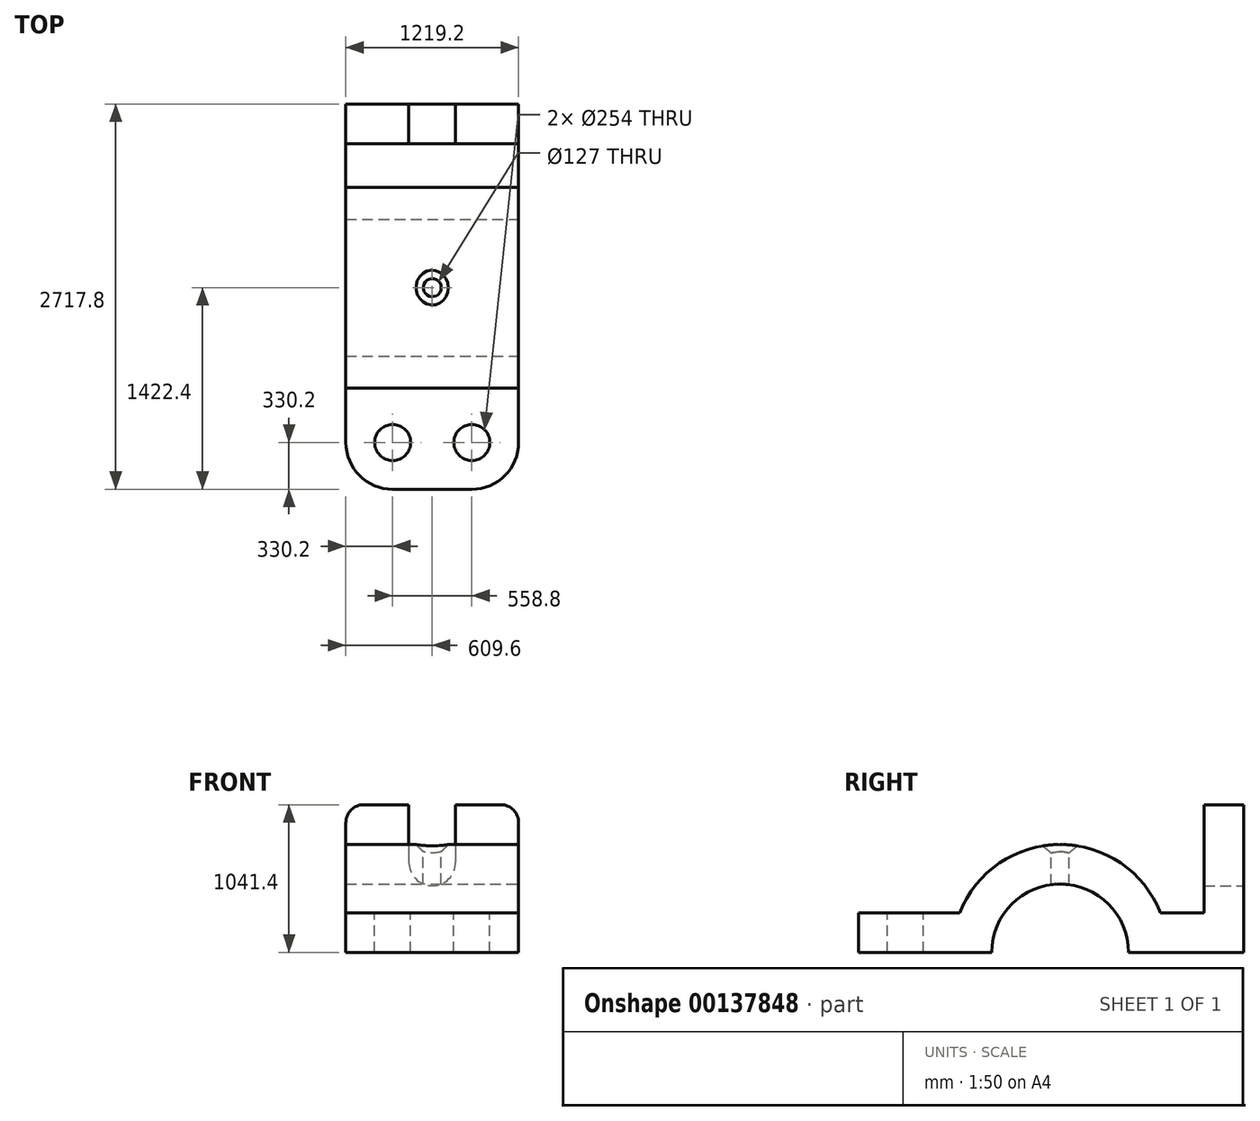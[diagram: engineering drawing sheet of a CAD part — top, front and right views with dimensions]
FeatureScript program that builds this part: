
annotation { "Feature Type Name" : "Feature", "Feature Type Description" : "" }
export const myFeature = defineFeature(function(context is Context, id is Id, definition is map)
    precondition{}
    {
        {
            var Q0;
            Q0=qCreatedBy(makeId("Top.planeOp"),FACE);
            var sketch = newSketch(context, id + "F0", { "sketchPlane" : qUnion([Q0])});
            skLineSegment(sketch, "E0", {"start": v(0, 0) * mm, "end": v(0, 2717.8) * mm});
            skLineSegment(sketch, "E1", {"start": v(0, 2717.8) * mm, "end": v(-1219.2, 2717.8) * mm});
            skLineSegment(sketch, "E2", {"start": v(-1219.2, 2717.8) * mm, "end": v(-1219.2, 0) * mm});
            skLineSegment(sketch, "E3", {"start": v(-1219.2, 0) * mm, "end": v(0, 0) * mm});
            skSolve(sketch);
        }
        {
            var Q0;
            Q0 = qSketchRegion(id + "F0", true);
            extrude(context, id + "F1", {"entities" : qUnion([Q0]), "depth" : 1041.4 * mm});
        }
        {
            var Q0;
            Q0=qCreatedBy(makeId("Right.planeOp"),FACE);
            var sketch = newSketch(context, id + "F2", { "sketchPlane" : qUnion([Q0])});
            skLineSegment(sketch, "E4", {"start": v(0, 0) * mm, "end": v(1422.4, 0) * mm});
            skLineSegment(sketch, "E5", {"start": v(1422.4, 0) * mm, "end": v(1905, 0) * mm});
            skLineSegment(sketch, "E6", {"start": v(1422.4, 0) * mm, "end": v(939.8, 0) * mm});
            skArc(sketch, "E7", {"start": v(1905, 0) * mm, "mid": v(1422.4, 481.35) * mm, "end": v(939.8, 0) * mm});
            skSolve(sketch);
        }
        {
            var Q0;
            Q0=makeQuery(id+"F2.imprint","IMPRINT",FACE,{"disambiguationData":[TD([[makeQuery(id+"F2.imprint","IMPRINT",EDGE,{"derivedFrom":sQuery(id+"F2.wireOp",EDGE,"E5")}),1.0]])]});
            extrude(context, id + "F3", {"entities" : qUnion([Q0]), "operationType" : NewBodyOperationType.REMOVE, "endBound" : BoundingType.THROUGH_ALL, "oppositeDirection" : true, "depth" : 25.4 * mm});
        }
        {
            var Q0;
            Q0=makeQuery(id+"F1.opExtrude","SWEPT_FACE",FACE,{"disambiguationData":[OSD([sQuery(id+"F0.wireOp",EDGE,"E0")])]});
            var sketch = newSketch(context, id + "F4", { "sketchPlane" : qUnion([Q0])});
            skLineSegment(sketch, "E8", {"start": v(0, 1041.4) * mm, "end": v(0, 279.4) * mm});
            skLineSegment(sketch, "E9", {"start": v(0, 279.4) * mm, "end": v(713.97, 279.4) * mm});
            skLineSegment(sketch, "E10", {"start": v(0, 1041.4) * mm, "end": v(2438.4, 1041.4) * mm});
            skLineSegment(sketch, "E11", {"start": v(2438.4, 1041.4) * mm, "end": v(2438.4, 279.4) * mm});
            skLineSegment(sketch, "E12", {"start": v(2438.4, 279.4) * mm, "end": v(2130.83, 279.4) * mm});
            skArc(sketch, "E13", {"start": v(2130.83, 279.4) * mm, "mid": v(1422.4, 760.75) * mm, "end": v(713.97, 279.4) * mm});
            skSolve(sketch);
        }
        {
            var Q0;
            Q0 = qSketchRegion(id + "F4", true);
            extrude(context, id + "F5", {"entities" : qUnion([Q0]), "operationType" : NewBodyOperationType.REMOVE, "endBound" : BoundingType.THROUGH_ALL, "oppositeDirection" : true, "depth" : 25.4 * mm});
        }
        {
            var Q0;
            Q0=makeQuery(id+"F5.boolean.opBoolean","COPY",FACE,{"derivedFrom":makeQuery(id+"F5.opExtrude","SWEPT_FACE",FACE,{"disambiguationData":[OSD([sQuery(id+"F4.wireOp",EDGE,"E9")])]})});
            var sketch = newSketch(context, id + "F6", { "sketchPlane" : qUnion([Q0])});
            skCircle(sketch, "E14", {"center": v(-889, 330.2) * mm, "radius": 127 * mm});
            skCircle(sketch, "E15", {"center": v(-330.2, 330.2) * mm, "radius": 127 * mm});
            skSolve(sketch);
        }
        {
            var Q0;
            Q0 = qSketchRegion(id + "F6", true);
            extrude(context, id + "F7", {"entities" : qUnion([Q0]), "operationType" : NewBodyOperationType.REMOVE, "endBound" : BoundingType.THROUGH_ALL, "oppositeDirection" : true, "depth" : 25.4 * mm});
        }
        {
            var Q0;
            Q0=makeQuery(id+"F1.opExtrude","SWEPT_EDGE",EDGE,{"disambiguationData":[OSD([sQuery(id+"F0.wireOp",EDGE,"E2"),sQuery(id+"F0.wireOp",EDGE,"E3")])]});
            var Q1;
            Q1=makeQuery(id+"F1.opExtrude","SWEPT_EDGE",EDGE,{"disambiguationData":[OSD([sQuery(id+"F0.wireOp",EDGE,"E0"),sQuery(id+"F0.wireOp",EDGE,"E3")])]});
            fillet(context, id + "F8", {"entities" : qUnion([Q0, Q1]), "radius" : 330.2 * mm, "tangentPropagation" : true, "allowEdgeOverflow" : false});
        }
        {
            var Q0;
            Q0=makeQuery(id+"F1.opExtrude","CAP_EDGE",EDGE,{"disambiguationData":[OSD([sQuery(id+"F0.wireOp",EDGE,"E0")])],"isStart":false});
            var Q1;
            Q1=makeQuery(id+"F1.opExtrude","CAP_EDGE",EDGE,{"disambiguationData":[OSD([sQuery(id+"F0.wireOp",EDGE,"E2")])],"isStart":false});
            fillet(context, id + "F9", {"entities" : qUnion([Q0, Q1]), "radius" : 127 * mm, "tangentPropagation" : true, "allowEdgeOverflow" : false});
        }
        {
            var Q0;
            Q0=makeQuery(id+"F1.opExtrude","SWEPT_FACE",FACE,{"disambiguationData":[OSD([sQuery(id+"F0.wireOp",EDGE,"E1")])]});
            var sketch = newSketch(context, id + "F10", { "sketchPlane" : qUnion([Q0])});
            skLineSegment(sketch, "E16", {"start": v(444.5, 1041.4) * mm, "end": v(444.5, 635) * mm});
            skLineSegment(sketch, "E17", {"start": v(774.7, 1041.4) * mm, "end": v(774.7, 635) * mm});
            skArc(sketch, "E18", {"start": v(774.7, 635) * mm, "mid": v(609.6, 469.9) * mm, "end": v(444.5, 635) * mm});
            skLineSegment(sketch, "E19", {"start": v(444.5, 1041.4) * mm, "end": v(774.7, 1041.4) * mm});
            skSolve(sketch);
        }
        {
            var Q0;
            Q0 = qSketchRegion(id + "F10", true);
            extrude(context, id + "F11", {"entities" : qUnion([Q0]), "operationType" : NewBodyOperationType.REMOVE, "oppositeDirection" : true, "depth" : 279.4 * mm});
        }
        {
            var Q0;
            Q0=qCreatedBy(makeId("Top.planeOp"),FACE);
            cPlane(context, id + "F12", {"entities" : qUnion([Q0]), "cplaneType" : CPlaneType.OFFSET, "offset" : 762 * mm, "width" : 152.4 * mm, "height" : 152.4 * mm});
        }
        {
            var Q0;
            Q0=qCreatedBy(id+"F12.planeOp",FACE);
            var sketch = newSketch(context, id + "F13", { "sketchPlane" : qUnion([Q0])});
            skCircle(sketch, "E20", {"center": v(-609.6, 1422.4) * mm, "radius": 127 * mm});
            skCircle(sketch, "E21", {"center": v(-609.6, 1422.4) * mm, "radius": 63.5 * mm});
            skSolve(sketch);
        }
        {
            var Q0;
            Q0=makeQuery(id+"F13.imprint","IMPRINT",FACE,{"disambiguationData":[TD([[makeQuery(id+"F13.imprint","IMPRINT",EDGE,{"derivedFrom":sQuery(id+"F13.wireOp",EDGE,"E21")}),1.0]])]});
            extrude(context, id + "F14", {"entities" : qUnion([Q0]), "operationType" : NewBodyOperationType.REMOVE, "endBound" : BoundingType.THROUGH_ALL, "oppositeDirection" : true, "depth" : 25.4 * mm});
        }
        {
            var Q0;
            Q0=makeQuery(id+"F14.boolean.opBoolean","INTERSECT",EDGE,{"derivedFrom":[makeQuery(id+"F5.boolean.opBoolean","COPY",FACE,{"derivedFrom":makeQuery(id+"F5.opExtrude","SWEPT_FACE",FACE,{"disambiguationData":[OSD([sQuery(id+"F4.wireOp",EDGE,"E13")])]})}),makeQuery(id+"F14.opExtrude","SWEPT_FACE",FACE,{"disambiguationData":[OSD([sQuery(id+"F13.wireOp",EDGE,"E21")])]})]});
            chamfer(context, id + "F15", {"entities" : qUnion([Q0]), "width" : 50.8 * mm, "tangentPropagation" : true});
        }
    });
